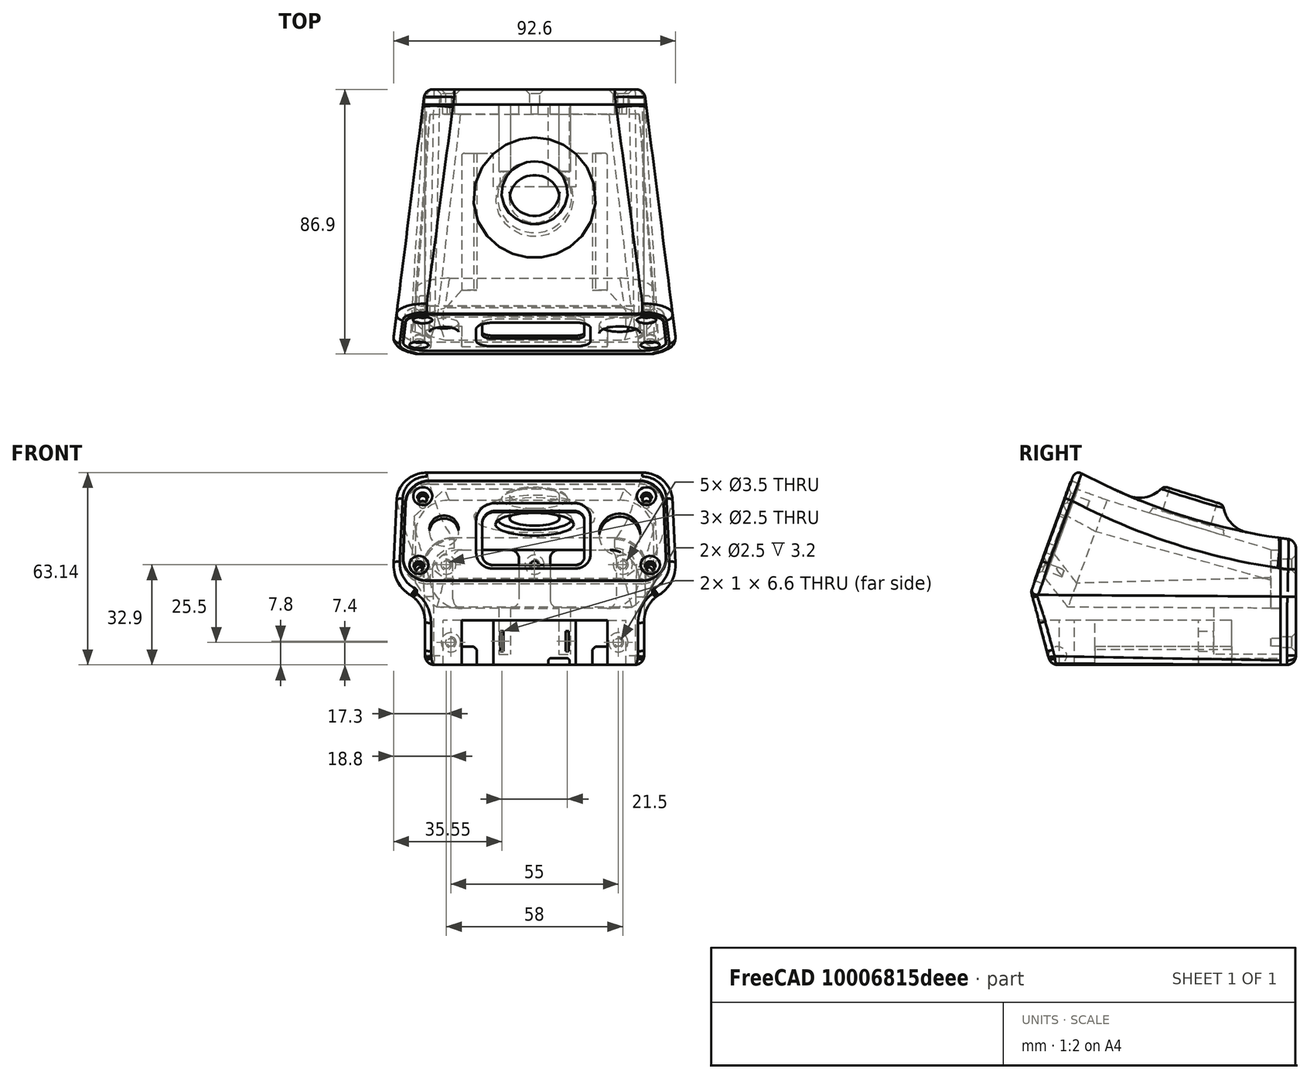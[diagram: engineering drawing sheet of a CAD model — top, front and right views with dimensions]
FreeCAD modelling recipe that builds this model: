
FCSTD DOCUMENT  (FreeCAD 2021.412R24301 +3461 (Git))
Label: solder_station4
License: All rights reserved
LicenseURL: http://en.wikipedia.org/wiki/All_rights_reserved
objects: Sketcher::SketchObject×18, PartDesign::Pocket×8, PartDesign::Fillet×6, Part::FeaturePython×3, App::DocumentObjectGroup×3, PartDesign::Chamfer×3, PartDesign::Body×3, PartDesign::FeatureBase×2, PartDesign::Pad×2, Mesh::Feature×2, Spreadsheet::Sheet×1, Part::Plane×1, Part::Loft×1, Part::Extrusion×1, Part::MultiCommon×1, PartDesign::SubtractiveLoft×1, PartDesign::Revolution×1, PartDesign::Groove×1, App::Part×1
note: 98 computed .brp shape members not serialized (recipe doc carries the construction recipe); baked Part::Feature solids carry a one-line shape summary decoded from their .brp

FEATURE [Sketcher::SketchObject] Sketch  label="RearSupport"
  AttachmentOffset = pos=(0,0,-37.8) rot=(0,0,1;0rad)
  FullyConstrained = true
  MapMode = 5
  Placement = pos=(0,37.8,8.4e-15) rot=(1,0,0;1.5708rad)
  Support = -> [XZ_Plane005]
  expr: .AttachmentOffset.Base.z = -<<param>>.mid_depth / 2 + <<param>>.wall
  expr: .Constraints[24] = 3
  expr: .Constraints[37] = <<param>>.bottom_height
  expr: .Constraints[38] = <<param>>.floor
  expr: .Constraints[39] = <<param>>.rear_height - <<param>>.wall
  expr: .Constraints[47] = <<param>>.reart_screw_width2
  expr: .Constraints[48] = <<param>>.rear_screw_width1
  expr: .Constraints[49] = <<param>>.screw_hole
  expr: .Constraints[50] = <<param>>.rear_screw_height
  expr: .Constraints[51] = <<param>>.rear_screw_height
  expr: .Constraints[52] = <<param>>.rear_screw_offset
  sketch-geometry (22):
    g0: LineSegment StartX=-23.8 StartY=13.8 StartZ=0 EndX=-8.1 EndY=13.8 EndZ=0
    g1: LineSegment StartX=26.8 StartY=10.8 StartZ=0 EndX=26.8 EndY=-2.4 EndZ=0
    g2: LineSegment StartX=23.8 StartY=-5.4 StartZ=0 EndX=8.1 EndY=-5.4 EndZ=0
    g3: LineSegment StartX=-26.8 StartY=-2.4 StartZ=0 EndX=-26.8 EndY=10.8 EndZ=0
    g4: LineSegment StartX=-5.1 StartY=10.8 StartZ=0 EndX=-5.1 EndY=-2.4 EndZ=0
    g5: LineSegment StartX=5.1 StartY=10.8 StartZ=0 EndX=5.1 EndY=-2.4 EndZ=0
    g6: LineSegment StartX=8.1 StartY=13.8 StartZ=0 EndX=23.8 EndY=13.8 EndZ=0
    g7: LineSegment StartX=-8.1 StartY=-5.4 StartZ=0 EndX=-23.8 EndY=-5.4 EndZ=0
    g8: ArcOfCircle CenterX=-8.1 CenterY=10.8 CenterZ=0 NormalX=0 NormalY=0 NormalZ=1 AngleXU=0 Radius=3 StartAngle=0 EndAngle=1.5708
    g9: ArcOfCircle CenterX=8.1 CenterY=10.8 CenterZ=0 NormalX=0 NormalY=0 NormalZ=1 AngleXU=0 Radius=3 StartAngle=1.5708 EndAngle=3.14159
    g10: ArcOfCircle CenterX=-8.1 CenterY=-2.4 CenterZ=0 NormalX=0 NormalY=0 NormalZ=1 AngleXU=0 Radius=3 StartAngle=4.71239 EndAngle=6.28319
    g11: ArcOfCircle CenterX=8.1 CenterY=-2.4 CenterZ=0 NormalX=0 NormalY=0 NormalZ=1 AngleXU=0 Radius=3 StartAngle=3.14159 EndAngle=4.71239
    g12: ArcOfCircle CenterX=-23.8 CenterY=10.8 CenterZ=0 NormalX=0 NormalY=0 NormalZ=1 AngleXU=0 Radius=3 StartAngle=1.5708 EndAngle=3.14159
    g13: ArcOfCircle CenterX=-23.8 CenterY=-2.4 CenterZ=0 NormalX=0 NormalY=0 NormalZ=1 AngleXU=0 Radius=3 StartAngle=3.14159 EndAngle=4.71239
    g14: ArcOfCircle CenterX=23.8 CenterY=10.8 CenterZ=0 NormalX=0 NormalY=0 NormalZ=1 AngleXU=0 Radius=3 StartAngle=0 EndAngle=1.5708
    g15: ArcOfCircle CenterX=23.8 CenterY=-2.4 CenterZ=0 NormalX=0 NormalY=0 NormalZ=1 AngleXU=0 Radius=3 StartAngle=4.71239 EndAngle=6.28319
    g16: Circle [constr] CenterX=0 CenterY=-24 CenterZ=0 NormalX=0 NormalY=0 NormalZ=1 AngleXU=0 Radius=3
    g17: Circle CenterX=0 CenterY=8.9 CenterZ=0 NormalX=0 NormalY=0 NormalZ=1 AngleXU=0 Radius=1.25
    g18: Circle CenterX=-29 CenterY=8.9 CenterZ=0 NormalX=0 NormalY=0 NormalZ=1 AngleXU=0 Radius=1.25
    g19: Circle CenterX=-27.5 CenterY=-16.6 CenterZ=0 NormalX=0 NormalY=0 NormalZ=1 AngleXU=0 Radius=1.25
    g20: Circle CenterX=27.5 CenterY=-16.6 CenterZ=0 NormalX=0 NormalY=0 NormalZ=1 AngleXU=0 Radius=1.25
    g21: Circle CenterX=29 CenterY=8.9 CenterZ=0 NormalX=0 NormalY=0 NormalZ=1 AngleXU=0 Radius=1.25
  constraints (53):
    c: Horizontal(g0)
    c: Horizontal(g2)
    c: Vertical(g1)
    c: Vertical(g3)
    c: Vertical(g4)
    c: Vertical(g5)
    c: Tangent(g0,g6)
    c: Tangent(g2,g7)
    c: Tangent(g0,g8) = 1.5708
    c: Tangent(g4,g8) = 1.5708
    c: Tangent(g5,g9) = -1.5708
    c: Tangent(g6,g9) = 1.5708
    c: Tangent(g7,g10) = 1.5708
    c: Tangent(g4,g10) = 1.5708
    c: Tangent(g5,g11) = -1.5708
    c: Tangent(g2,g11) = 1.5708
    c: Tangent(g0,g12) = 1.5708
    c: Tangent(g3,g12) = 1.5708
    c: Tangent(g3,g13) = 1.5708
    c: Tangent(g7,g13) = 1.5708
    c: Tangent(g6,g14) = 1.5708
    c: Tangent(g1,g14) = 1.5708
    c: Tangent(g1,g15) = 1.5708
    c: Tangent(g2,g15) = 1.5708
    c: Radius(g9) = 3
    c: Equal(g12,g13)
    c: Equal(g13,g10)
    c: Equal(g10,g8)
    c: Equal(g11,g15)
    c: Equal(g15,g14)
    c: Equal(g14,g9)
    c: DistanceX(g4,g-1) = 5.1
    c: DistanceX(g5,g1) = 21.7
    c: Symmetric(g4,g5,g-2)
    c: Equal(g7,g2)
    c: PointOnObject(g16,g-2)
    c: Radius(g16) = 3
    c: DistanceY(g16,g-1) = 24
    c: DistanceY(g16,g2) = 18.6
    c: DistanceY(g16,g6) = 37.8
    c: PointOnObject(g17,g-2)
    c: Equal(g21,g18)
    c: Equal(g18,g19)
    c: Equal(g19,g20)
    c: Equal(g18,g17)
    c: Symmetric(g20,g19,g-2)
    c: Symmetric(g18,g21,g-2)
    c: DistanceX(g19,g20) = 55
    c: DistanceX(g18,g21) = 58
    c: Diameter(g19) = 2.5
    c: DistanceY(g20,g21) = 25.5
    c: DistanceY(g20,g17) = 25.5
    c: DistanceY(g16,g19) = 7.4
FEATURE [Spreadsheet::Sheet] Spreadsheet  label="param"
  PythonMode = false
  cells = A1=Body; B2=top_depth; C2(top_depth)=70; B3=mid_depth; C3(mid_depth)=82; D3=half is rear reference; B4=bottom_depth; C4(bottom_depth)=75; B6=bottom_width; C6(bottom_width)=72; B7=bottom_height; C7(bottom_height)=24; B8=bottom_angle; C8(bottom_angle)=15; B10=rear_width; C10(rear_width)=72; B11=rear_height; C11(rear_height)=41; B13=mid_width; C13(mid_width)=80; B14=mid_height; C14(mid_height)=50; B16=front_width1; C16(front_width1)=91; D16=@top; E16=upper; B17=front_width2; C17(front_width2)=94; D17=@mid; E17=lower; B18=front_height; C18(front_height)=64; B19=front_angle; C19(front_angle)=20; B21=wall; C21(wall)=3.2; B22=radius_big; C22(radius_big)=10; B23=radius_small; C23(radius_small)=3; B24=arch; C24(arch)=200; A26=Button; B27=button_offset; C27(button_offset)=10; B28=button_inside_dia; C28(button_inside_dia)=20; B29=button_outside_dia; C29(button_outside_dia)=22; B30=button_height; C30(button_height)=24; B31=button_extension; C31(button_extension)=8; B32=button_fillet; C32(button_fillet)=12; B33=button_angle; C33(button_angle)=-17; B34=button_hole; C34(button_hole)=16.4; B35=button_hole_center; C35(button_hole_center)=-0.5; A37=Battery Cuts; B38=batt_carveout; C38(batt_carveout)=14.6; B39=batt_rail; C39(batt_rail)=6; B40=batt_rail_length; C40(batt_rail_length)=45; A42=Terminals; B43=terminal_height; C43(terminal_height)=6.6; B44=terminal_thickness; C44(terminal_thickness)=1; B45=terminal_seperation; C45(terminal_seperation)=21.5; B46=terminal_offset; C46(terminal_offset)=4.5; B47=terminal_depth; C47(terminal_depth)=22; A49=Box Interior; B50=floor; C50(floor)=18.6; B51=rear_inside_width; C51(rear_inside_width)==C10 - C21; D51=calc; B52=rear_inside_height; C52(rear_inside_height)==C11 - C21; D52=calc; B53=mid_inside_width; C53(mid_inside_width)==C13; D53=calc; B54=mid_inside_height; C54(mid_inside_height)==C14 + 6; D54=calc; B55=front_inside_width1; C55(front_inside_width1)==C62 - C58 * 2; D55=calc; E55=upper; B56=front_inside_width2; C56(front_inside_width2)==C63 - C58 * 2; D56=calc; E56=lower; B57=front_inside_height; C57(front_inside_height)==C64 - C59 * 2; D57=calc; B58=front_width_lip_width; C58(front_width_lip_width)=3; B59=front_inside_lip_height; C59(front_inside_lip_height)=2; A61=Face; B62=face_width1; C62(face_width1)==84 + 1; B63=face_width2; C63(face_width2)==85.5 + 1; B64=face_height; C64(face_height)==34 + 1; B65=face_thickness; C65(face_thickness)=3; B66=face_radius; C66(face_radius)=8; B67=face_offset; C67(face_offset)=2.8; D67=2.8; A69=Screws; B70=screw_hole; C70(screw_hole)=2.5; B72=front_screw_width1; C72(front_screw_width1)=73.5; D72=upper; B73=front_screw_width2; C73(front_screw_width2)=76; D73=lower; B74=front_screw_height; C74(front_screw_height)=24; B75=front_screw_offset; C75(front_screw_offset)=5.5; B77=rear_screw_width1; C77(rear_screw_width1)=58; B78=reart_screw_width2; C78(reart_screw_width2)=55; B79=rear_screw_height; C79(rear_screw_height)=25.5; B80=rear_screw_offset; C80(rear_screw_offset)=7.4; A82=Back; B83=back_thickness; C83(back_thickness)=5
FEATURE [Sketcher::SketchObject] Sketch008  label="SketchButtonHole"
  AttachmentOffset = pos=(0,-0.5,24) rot=(1,0,0;-0.296706rad)
  FullyConstrained = true
  MapMode = 5
  Placement = pos=(0,-0.5,24) rot=(1,0,0;5.98648rad)
  Support = -> [XY_Plane005]
  expr: .AttachmentOffset.Base.y = <<param>>.button_hole_center
  expr: .AttachmentOffset.Base.z = <<param>>.button_height
  expr: .AttachmentOffset.Rotation.Angle = <<param>>.button_angle
  expr: .Constraints[0] = <<param>>.button_hole
  expr: .Constraints[2] = <<param>>.button_offset
  sketch-geometry (1):
    g0: Circle CenterX=0 CenterY=10 CenterZ=0 NormalX=0 NormalY=0 NormalZ=1 AngleXU=0 Radius=8.2
  constraints (3):
    c: Diameter(g0) = 16.4
    c: PointOnObject(g0,g-2)
    c: DistanceY(g-1,g0) = 10
FEATURE [Sketcher::SketchObject] Sketch012  label="SketchSide"
  AttachmentOffset = pos=(2.5,0,0) rot=(0,0,1;0rad)
  FullyConstrained = true
  MapMode = 5
  Placement = pos=(6e-16,2.5,-6e-16) rot=(0.57735,0.57735,0.57735;2.0944rad)
  Support = -> [YZ_Plane006]
  expr: .AttachmentOffset.Base.x = <<param>>.back_thickness / 2
  expr: .Constraints[14] = <<param>>.bottom_height
  expr: .Constraints[15] = <<param>>.radius_small
  expr: .Constraints[16] = 90 - <<param>>.bottom_angle
  expr: .Constraints[17] = 90 - <<param>>.front_angle
  expr: .Constraints[21] = <<param>>.front_height
  expr: .Constraints[4] = <<param>>.rear_height - <<param>>.bottom_height
  expr: .Constraints[5] = <<param>>.arch
  expr: .Constraints[6] = <<param>>.mid_depth + <<param>>.back_thickness
  sketch-geometry (7):
    g0: LineSegment StartX=43.5 StartY=0 StartZ=0 EndX=43.5 EndY=17 EndZ=0
    g1: LineSegment StartX=-43.5 StartY=0 StartZ=0 EndX=-28.9412 EndY=40 EndZ=0
    g2: ArcOfCircle CenterX=66.6993 CenterY=215.65 CenterZ=0 NormalX=0 NormalY=0 NormalZ=1 AngleXU=0 Radius=200 StartAngle=4.21378 EndAngle=4.59613
    g3: LineSegment StartX=-43.5 StartY=0 StartZ=0 EndX=-37.665 EndY=-21.7765 EndZ=0
    g4: LineSegment StartX=-34.7673 StartY=-24 StartZ=0 EndX=43.5 EndY=-24 EndZ=0
    g5: LineSegment StartX=43.5 StartY=-24 StartZ=0 EndX=43.5 EndY=0 EndZ=0
    g6: ArcOfCircle CenterX=-34.7672 CenterY=-21 CenterZ=0 NormalX=0 NormalY=0 NormalZ=1 AngleXU=0 Radius=3 StartAngle=3.4034 EndAngle=4.71238
  constraints (22):
    c: PointOnObject(g1,g-1)
    c: Vertical(g0)
    c: Coincident(g2,g0)
    c: Symmetric(g1,g0,g-2)
    c: DistanceY(g0,g0) = 17
    c: Radius(g2) = 200
    c: DistanceX(g1,g0) = 87
    c: Horizontal(g4)
    c: Coincident(g5,g4)
    c: Vertical(g5)
    c: Coincident(g6,g3)
    c: Coincident(g6,g4)
    c: Tangent(g6,g4)
    c: Tangent(g6,g3)
    c: DistanceY(g4,g-1) = 24
    c: Radius(g6) = 3
    c: Angle(g3,g-1) = 1.309
    c: Angle(g-1,g1) = 1.22173
    c: Coincident(g3,g1)
    c: Coincident(g5,g0)
    c: Coincident(g2,g1)
    c: DistanceY(g4,g1) = 64
FEATURE [Sketcher::SketchObject] Sketch018  label="SketchBat1"
  AttachmentOffset = pos=(0,0,-24) rot=(0,0,1;0rad)
  FullyConstrained = true
  MapMode = 5
  Placement = pos=(0,0,-24) rot=(0,0,1;0rad)
  Support = -> [XY_Plane005]
  expr: .AttachmentOffset.Base.z = -<<param>>.bottom_height
  expr: .Constraints[63] = <<param>>.batt_rail_length
  expr: .Constraints[64] = <<param>>.mid_depth / 2
  sketch-geometry (21):
    g0: LineSegment StartX=-24 StartY=-41.7082 StartZ=0 EndX=24 EndY=-41.7082 EndZ=0
    g1: LineSegment StartX=24 StartY=-41.7082 StartZ=0 EndX=24 EndY=-31.7082 EndZ=0
    g2: LineSegment StartX=24 StartY=-31.7082 StartZ=0 EndX=30 EndY=-31.7082 EndZ=0
    g3: LineSegment StartX=30 StartY=-31.7082 StartZ=0 EndX=30 EndY=-26.7082 EndZ=0
    g4: LineSegment StartX=30 StartY=-26.7082 StartZ=0 EndX=24 EndY=-20 EndZ=0
    g5: LineSegment StartX=24 StartY=-20 StartZ=0 EndX=24 EndY=24 EndZ=0
    g6: LineSegment StartX=13.5 StartY=24 StartZ=0 EndX=13.5 EndY=14 EndZ=0
    g7: LineSegment StartX=13.5 StartY=14 StartZ=0 EndX=-13.5 EndY=14 EndZ=0
    g8: LineSegment StartX=-13.5 StartY=14 StartZ=0 EndX=-13.5 EndY=24 EndZ=0
    g9: LineSegment StartX=-24 StartY=24 StartZ=0 EndX=-24 EndY=-20 EndZ=0
    g10: LineSegment StartX=-24 StartY=-20 StartZ=0 EndX=-30 EndY=-26.7082 EndZ=0
    g11: LineSegment StartX=-30 StartY=-26.7082 StartZ=0 EndX=-30 EndY=-31.7082 EndZ=0
    g12: LineSegment StartX=-30 StartY=-31.7082 StartZ=0 EndX=-24 EndY=-31.7082 EndZ=0
    g13: LineSegment StartX=-24 StartY=-31.7082 StartZ=0 EndX=-24 EndY=-41.7082 EndZ=0
    g14: Circle [constr] CenterX=0 CenterY=41 CenterZ=0 NormalX=0 NormalY=0 NormalZ=1 AngleXU=0 Radius=4
    g15: ArcOfCircle CenterX=-14.5 CenterY=24 CenterZ=0 NormalX=0 NormalY=0 NormalZ=1 AngleXU=0 Radius=1 StartAngle=6.28318 EndAngle=7.85399
    g16: LineSegment StartX=-23 StartY=25 StartZ=0 EndX=-14.5 EndY=25 EndZ=0
    g17: LineSegment StartX=14.5 StartY=25 StartZ=0 EndX=23 EndY=25 EndZ=0
    g18: ArcOfCircle CenterX=-23 CenterY=24 CenterZ=0 NormalX=0 NormalY=0 NormalZ=1 AngleXU=0 Radius=1 StartAngle=1.57079 EndAngle=3.1416
    g19: ArcOfCircle CenterX=14.5 CenterY=24 CenterZ=0 NormalX=0 NormalY=0 NormalZ=1 AngleXU=0 Radius=1 StartAngle=1.5708 EndAngle=3.14159
    g20: ArcOfCircle CenterX=23 CenterY=24 CenterZ=0 NormalX=0 NormalY=0 NormalZ=1 AngleXU=0 Radius=1.00001 StartAngle=2.75124e-06 EndAngle=1.5708
  constraints (65):
    c: Horizontal(g0)
    c: Coincident(g1,g0)
    c: Vertical(g1)
    c: Coincident(g2,g1)
    c: Horizontal(g2)
    c: Coincident(g3,g2)
    c: Coincident(g3,g4)
    c: Vertical(g5)
    c: Coincident(g6,g7)
    c: Coincident(g7,g8)
    c: Vertical(g8)
    c: Vertical(g9)
    c: Coincident(g10,g11)
    c: Vertical(g11)
    c: Coincident(g11,g12)
    c: Horizontal(g12)
    c: Coincident(g12,g13)
    c: Equal(g6,g8)
    c: Equal(g5,g9)
    c: Equal(g4,g10)
    c: Equal(g3,g11)
    c: Equal(g12,g2)
    c: Equal(g1,g13)
    c: Coincident(g13,g0)
    c: Vertical(g13)
    c: DistanceX(g7,g7) = 27
    c: Symmetric(g7,g6,g-2)
    c: Distance(g4) = 9
    c: Vertical(g3)
    c: DistanceY(g3,g3) = 5
    c: DistanceX(g2,g2) = 6
    c: DistanceY(g1,g1) = 10
    c: DistanceX(g0,g0) = 48
    c: PointOnObject(g14,g-2)
    c: Coincident(g9,g10)
    c: Coincident(g5,g4)
    c: Coincident(g15,g8)
    c: Coincident(g16,g15)
    c: Tangent(g15,g8)
    c: Horizontal(g16)
    c: Horizontal(g17)
    c: DistanceX(g9,g5) = 48
    c: Symmetric(g4,g9,g-2)
    c: Equal(g16,g17)
    c: Coincident(g18,g9)
    c: Coincident(g18,g16)
    c: Equal(g18,g15)
    c: Tangent(g18,g16)
    c: Tangent(g18,g9)
    c: DistanceY(g6,g17) = 11
    c: Vertical(g6)
    c: Coincident(g19,g6)
    c: Coincident(g19,g17)
    c: Coincident(g20,g17)
    c: Coincident(g20,g5)
    c: Tangent(g20,g17)
    c: Tangent(g20,g5)
    c: Tangent(g19,g6)
    c: Tangent(g19,g17)
    c: Equal(g15,g19)
    c: Radius(g19) = 1
    c: Radius(g14) = 4
    c: DistanceY(g15,g14) = 16
    c: DistanceY(g9,g16) = 45
    c: DistanceY(g-1,g14) = 41
FEATURE [Sketcher::SketchObject] Sketch019  label="SketchBat2"
  AttachmentOffset = pos=(0,0,-25) rot=(0,0,1;0rad)
  FullyConstrained = true
  MapMode = 5
  Placement = pos=(0,25,5.6e-15) rot=(1,0,0;1.5708rad)
  Support = -> [XZ_Plane005]
  expr: .AttachmentOffset.Base.z = -<<param>>.mid_depth / 2 + 16
  expr: .Constraints[17] = <<param>>.bottom_height
  expr: .Constraints[18] = <<param>>.batt_rail
  expr: .Constraints[19] = 48.01mm
  sketch-geometry (10):
    g0: LineSegment StartX=-24.005 StartY=-18 StartZ=0 EndX=-20.005 EndY=-18 EndZ=0
    g1: LineSegment StartX=-19.005 StartY=-24 StartZ=0 EndX=-24.005 EndY=-24 EndZ=0
    g2: LineSegment StartX=-24.005 StartY=-24 StartZ=0 EndX=-24.005 EndY=-18 EndZ=0
    g3: LineSegment StartX=24.005 StartY=-18 StartZ=0 EndX=20.005 EndY=-18 EndZ=0
    g4: LineSegment StartX=19.005 StartY=-24 StartZ=0 EndX=24.005 EndY=-24 EndZ=0
    g5: LineSegment StartX=24.005 StartY=-24 StartZ=0 EndX=24.005 EndY=-18 EndZ=0
    g6: LineSegment StartX=-19.005 StartY=-19 StartZ=0 EndX=-19.005 EndY=-24 EndZ=0
    g7: LineSegment StartX=19.005 StartY=-24 StartZ=0 EndX=19.005 EndY=-19 EndZ=0
    g8: LineSegment StartX=-20.005 StartY=-18 StartZ=0 EndX=-19.005 EndY=-19 EndZ=0
    g9: LineSegment StartX=19.005 StartY=-19 StartZ=0 EndX=20.005 EndY=-18 EndZ=0
  constraints (29):
    c: Coincident(g1,g2)
    c: Coincident(g2,g0)
    c: Horizontal(g0)
    c: Horizontal(g1)
    c: Vertical(g2)
    c: Coincident(g4,g5)
    c: Coincident(g5,g3)
    c: Horizontal(g3)
    c: Horizontal(g4)
    c: Vertical(g5)
    c: Coincident(g6,g1)
    c: Vertical(g6)
    c: Equal(g1,g4)
    c: Coincident(g7,g4)
    c: Vertical(g7)
    c: Equal(g6,g7)
    c: Symmetric(g1,g4,g-2)
    c: DistanceY(g1,g-1) = 24
    c: DistanceY(g4,g3) = 6
    c: DistanceX(g1,g4) = 48.01
    c: DistanceX(g4,g4) = 5
    c: Coincident(g8,g0)
    c: Coincident(g8,g6)
    c: Coincident(g9,g7)
    c: Coincident(g9,g3)
    c: Equal(g0,g3)
    c: Equal(g2,g5)
    c: DistanceX(g0,g0) = 4
    c: DistanceY(g1,g6) = 5
FEATURE [Sketcher::SketchObject] Sketch021  label="SketchButton"
  AttachmentOffset = pos=(10,24,0) rot=(0,0,1;-0.296706rad)
  FullyConstrained = true
  MapMode = 5
  Placement = pos=(-3.1e-15,10,24) rot=(-0.51122,-0.690875,-0.51122;4.35074rad)
  Support = -> [YZ_Plane005]
  expr: .AttachmentOffset.Base.x = <<param>>.button_offset
  expr: .AttachmentOffset.Base.y = <<param>>.button_height
  expr: .AttachmentOffset.Rotation.Angle = <<param>>.button_angle
  expr: .Constraints[6] = <<param>>.button_extension
  expr: .Constraints[7] = <<param>>.button_outside_dia / 2
  sketch-geometry (5):
    g0: LineSegment StartX=0 StartY=0 StartZ=0 EndX=0 EndY=8 EndZ=0
    g1: LineSegment StartX=0 StartY=8 StartZ=0 EndX=9 EndY=8 EndZ=0
    g2: LineSegment StartX=0 StartY=0 StartZ=0 EndX=11 EndY=0 EndZ=0
    g3: LineSegment StartX=11 StartY=0 StartZ=0 EndX=11 EndY=6 EndZ=0
    g4: ArcOfCircle CenterX=9 CenterY=6 CenterZ=0 NormalX=0 NormalY=0 NormalZ=1 AngleXU=0 Radius=2 StartAngle=1.123e-13 EndAngle=1.5708
  constraints (13):
    c: Coincident(g0,g-1)
    c: PointOnObject(g0,g-2)
    c: Coincident(g1,g0)
    c: Horizontal(g1)
    c: Coincident(g2,g0)
    c: Horizontal(g2)
    c: DistanceY(g0,g0) = 8
    c: DistanceX(g2,g2) = 11
    c: Coincident(g3,g2)
    c: Vertical(g3)
    c: Radius(g4) = 2
    c: Tangent(g4,g3) = -1.5708
    c: Tangent(g4,g1) = 1.5708
FEATURE [Sketcher::SketchObject] Sketch022  label="SketchRearInside"
  AttachmentOffset = pos=(0,0,-37.8) rot=(0,0,1;0rad)
  FullyConstrained = true
  MapMode = 5
  Placement = pos=(0,37.8,8.4e-15) rot=(1,0,0;1.5708rad)
  Support = -> [XZ_Plane005]
  expr: .AttachmentOffset.Base.z = -<<param>>.mid_depth / 2 + <<param>>.wall
  expr: .Constraints[12] = <<param>>.radius_big
  expr: .Constraints[18] = <<param>>.rear_inside_width
  expr: .Constraints[26] = <<param>>.bottom_height
  expr: .Constraints[27] = <<param>>.rear_inside_height
  expr: .Constraints[29] = <<param>>.floor
  sketch-geometry (9):
    g0: LineSegment StartX=-34.4 StartY=3.80003 StartZ=0 EndX=-34.4 EndY=4.59997 EndZ=0
    g1: LineSegment StartX=-24.4 StartY=-5.4 StartZ=0 EndX=24.4 EndY=-5.4 EndZ=0
    g2: LineSegment StartX=34.4 StartY=4.59997 StartZ=0 EndX=34.4 EndY=3.80003 EndZ=0
    g3: LineSegment StartX=-24.4 StartY=13.8 StartZ=0 EndX=24.4 EndY=13.8 EndZ=0
    g4: ArcOfCircle CenterX=24.4 CenterY=3.8 CenterZ=0 NormalX=0 NormalY=0 NormalZ=1 AngleXU=0 Radius=10 StartAngle=3.49138e-06 EndAngle=1.57079
    g5: ArcOfCircle CenterX=24.4 CenterY=4.6 CenterZ=0 NormalX=0 NormalY=0 NormalZ=1 AngleXU=0 Radius=10 StartAngle=4.71239 EndAngle=6.28318
    g6: ArcOfCircle CenterX=-24.4 CenterY=3.8 CenterZ=0 NormalX=0 NormalY=0 NormalZ=1 AngleXU=0 Radius=10 StartAngle=1.5708 EndAngle=3.14159
    g7: ArcOfCircle CenterX=-24.4 CenterY=4.6 CenterZ=0 NormalX=0 NormalY=0 NormalZ=1 AngleXU=0 Radius=10 StartAngle=3.1416 EndAngle=4.71239
    g8: Circle [constr] CenterX=0 CenterY=-24 CenterZ=0 NormalX=0 NormalY=0 NormalZ=1 AngleXU=0 Radius=3
  constraints (30):
    c: Vertical(g0)
    c: Horizontal(g1)
    c: Vertical(g2)
    c: Horizontal(g3)
    c: Equal(g3,g1)
    c: Equal(g0,g2)
    c: Coincident(g4,g3)
    c: Coincident(g4,g2)
    c: Coincident(g5,g2)
    c: Coincident(g5,g1)
    c: Coincident(g6,g0)
    c: Coincident(g6,g3)
    c: Radius(g6) = 10
    c: Equal(g6,g4)
    c: Equal(g4,g5)
    c: Coincident(g7,g1)
    c: Coincident(g7,g0)
    c: Equal(g5,g7)
    c: DistanceX(g0,g2) = 68.8
    c: Symmetric(g0,g2,g-2)
    c: Tangent(g4,g2)
    c: Tangent(g4,g3)
    c: Tangent(g5,g2)
    c: Tangent(g5,g1)
    c: Tangent(g6,g3)
    c: PointOnObject(g8,g-2)
    c: DistanceY(g8,g-1) = 24
    c: DistanceY(g8,g3) = 37.8
    c: Radius(g8) = 3
    c: DistanceY(g8,g1) = 18.6
FEATURE [Sketcher::SketchObject] Sketch023  label="SketchFrontInside"
  AttachmentOffset = pos=(0,0,38) rot=(1,0,0;-0.349066rad)
  FullyConstrained = true
  MapMode = 5
  Placement = pos=(0,-38,-8.4e-15) rot=(-1,0,0;5.06145rad)
  Support = -> [XZ_Plane005]
  expr: .AttachmentOffset.Base.z = <<param>>.mid_depth / 2 - <<param>>.face_thickness
  expr: .AttachmentOffset.Rotation.Angle = -<<param>>.front_angle
  expr: .Constraints[19] = <<param>>.front_inside_width2
  expr: .Constraints[1] = <<param>>.front_inside_width1
  expr: .Constraints[20] = <<param>>.front_inside_width2 / 2
  expr: .Constraints[21] = <<param>>.face_offset + <<param>>.front_inside_lip_height
  expr: .Constraints[2] = <<param>>.front_inside_height
  sketch-geometry (8):
    g0: LineSegment StartX=-29.5 StartY=4.8 StartZ=0 EndX=29.5 EndY=4.8 EndZ=0
    g1: LineSegment StartX=29.5 StartY=35.8 StartZ=0 EndX=-29.5 EndY=35.8 EndZ=0
    g2: LineSegment StartX=-39.5 StartY=26.3677 StartZ=0 EndX=-40.25 EndY=13.3677 EndZ=0
    g3: LineSegment StartX=-39.5 StartY=26.3677 StartZ=0 EndX=-29.5 EndY=35.8 EndZ=0
    g4: LineSegment StartX=29.5 StartY=35.8 StartZ=0 EndX=39.5 EndY=26.3677 EndZ=0
    g5: LineSegment StartX=40.25 StartY=13.3677 StartZ=0 EndX=29.5 EndY=4.8 EndZ=0
    g6: LineSegment StartX=-40.25 StartY=13.3677 StartZ=0 EndX=-29.5 EndY=4.8 EndZ=0
    g7: LineSegment StartX=39.5 StartY=26.3677 StartZ=0 EndX=40.25 EndY=13.3677 EndZ=0
  constraints (22):
    c: Symmetric(g0,g0,g-2)
    c: DistanceX(g2,g4) = 79
    c: DistanceY(g0,g1) = 31
    c: Symmetric(g1,g1,g-2)
    c: Coincident(g3,g2)
    c: Coincident(g3,g1)
    c: Coincident(g4,g1)
    c: Coincident(g5,g0)
    c: Coincident(g6,g2)
    c: Coincident(g6,g0)
    c: Equal(g3,g6)
    c: Equal(g6,g5)
    c: Equal(g5,g4)
    c: Coincident(g7,g4)
    c: Coincident(g7,g5)
    c: DistanceY(g7,g7) = 13
    c: Equal(g7,g2)
    c: Equal(g1,g0)
    c: DistanceX(g1,g1) = 59
    c: DistanceX(g2,g5) = 80.5
    c: DistanceX(g2,g-1) = 40.25
    c: DistanceY(g-1,g0) = 4.8
FEATURE [Sketcher::SketchObject] Sketch024  label="SketchFaceCut"
  AttachmentOffset = pos=(0,0,38) rot=(1,0,0;-0.349066rad)
  FullyConstrained = true
  MapMode = 5
  Placement = pos=(0,-38,-8.4e-15) rot=(-1,0,0;5.06145rad)
  Support = -> [XZ_Plane005]
  expr: .AttachmentOffset.Base.z = <<param>>.mid_depth / 2 - <<param>>.face_thickness
  expr: .AttachmentOffset.Rotation.Angle = -<<param>>.front_angle
  expr: .Constraints[13] = <<param>>.face_radius
  expr: .Constraints[22] = <<param>>.face_width1
  expr: .Constraints[23] = <<param>>.face_width2
  expr: .Constraints[24] = <<param>>.face_offset
  expr: .Constraints[25] = <<param>>.face_height
  sketch-geometry (8):
    g0: LineSegment StartX=-34.5062 StartY=37.8 StartZ=0 EndX=34.5063 EndY=37.8 EndZ=0
    g1: LineSegment StartX=42.5001 StartY=30.1155 StartZ=0 EndX=43.25 EndY=11.1155 EndZ=0
    g2: LineSegment StartX=35.2562 StartY=2.8 StartZ=0 EndX=-35.2562 EndY=2.8 EndZ=0
    g3: LineSegment StartX=-43.25 StartY=11.1156 StartZ=0 EndX=-42.4999 EndY=30.1156 EndZ=0
    g4: ArcOfCircle CenterX=34.5063 CenterY=29.8 CenterZ=0 NormalX=0 NormalY=0 NormalZ=1 AngleXU=0 Radius=8 StartAngle=0.0394514 EndAngle=1.5708
    g5: ArcOfCircle CenterX=35.2563 CenterY=10.8 CenterZ=0 NormalX=0 NormalY=0 NormalZ=1 AngleXU=0 Radius=8 StartAngle=4.71239 EndAngle=6.32264
    g6: ArcOfCircle CenterX=-34.5062 CenterY=29.8 CenterZ=0 NormalX=0 NormalY=0 NormalZ=1 AngleXU=0 Radius=8 StartAngle=1.5708 EndAngle=3.10214
    g7: ArcOfCircle CenterX=-35.2562 CenterY=10.8 CenterZ=0 NormalX=0 NormalY=0 NormalZ=1 AngleXU=0 Radius=8 StartAngle=3.10214 EndAngle=4.71239
  constraints (27):
    c: Horizontal(g0)
    c: Coincident(g4,g0)
    c: Coincident(g4,g1)
    c: Coincident(g5,g1)
    c: Coincident(g5,g2)
    c: Coincident(g6,g0)
    c: Coincident(g6,g3)
    c: Coincident(g7,g3)
    c: Coincident(g7,g2)
    c: Equal(g1,g3)
    c: Equal(g4,g6)
    c: Equal(g6,g7)
    c: Equal(g7,g5)
    c: Radius(g4) = 8
    c: Tangent(g6,g3)
    c: Tangent(g7,g3)
    c: Tangent(g7,g2)
    c: Tangent(g6,g0)
    c: Tangent(g4,g0)
    c: Tangent(g4,g1)
    c: Tangent(g5,g1)
    c: Tangent(g5,g2)
    c: DistanceX(g3,g1) = 85
    c: DistanceX(g3,g1) = 86.5
    c: DistanceY(g-1,g2) = 2.8
    c: DistanceY(g2,g0) = 35
    c: Symmetric(g2,g2,g-2)
FEATURE [Sketcher::SketchObject] Sketch025  label="SketchMidInside"
  AttachmentOffset = pos=(0,0,27) rot=(1,0,0;-0.349066rad)
  FullyConstrained = true
  MapMode = 5
  Placement = pos=(0,-27,-6e-15) rot=(-1,0,0;5.06145rad)
  Support = -> [XZ_Plane005]
  expr: .AttachmentOffset.Base.z = <<param>>.mid_depth / 2 - 14
  expr: .AttachmentOffset.Rotation.Angle = -<<param>>.front_angle
  expr: .Constraints[10] = <<param>>.radius_big + 1
  expr: .Constraints[11] = <<param>>.floor
  expr: .Constraints[12] = Spreadsheet.mid_inside_width - 2
  expr: .Constraints[14] = <<param>>.mid_inside_height
  expr: .Constraints[23] = <<param>>.mid_width - 16
  expr: .Constraints[4] = <<param>>.bottom_height
  sketch-geometry (9):
    g0: LineSegment StartX=-28 StartY=32 StartZ=0 EndX=28 EndY=32 EndZ=0
    g1: LineSegment StartX=39 StartY=21 StartZ=0 EndX=39 EndY=3 EndZ=0
    g2: LineSegment StartX=32 StartY=-5.4 StartZ=0 EndX=-32 EndY=-5.4 EndZ=0
    g3: LineSegment StartX=-39 StartY=3 StartZ=0 EndX=-39 EndY=21 EndZ=0
    g4: Circle [constr] CenterX=0 CenterY=-24 CenterZ=0 NormalX=0 NormalY=0 NormalZ=1 AngleXU=0 Radius=3
    g5: ArcOfCircle CenterX=-28 CenterY=21 CenterZ=0 NormalX=0 NormalY=0 NormalZ=1 AngleXU=0 Radius=11 StartAngle=1.5708 EndAngle=3.14159
    g6: ArcOfCircle CenterX=28 CenterY=21 CenterZ=0 NormalX=0 NormalY=0 NormalZ=1 AngleXU=0 Radius=11 StartAngle=0 EndAngle=1.5708
    g7: ArcOfCircle CenterX=-17.5474 CenterY=13.7605 CenterZ=0 NormalX=0 NormalY=0 NormalZ=1 AngleXU=0 Radius=24 StartAngle=3.60651 EndAngle=4.06615
    g8: ArcOfCircle CenterX=17.5474 CenterY=13.7605 CenterZ=0 NormalX=0 NormalY=0 NormalZ=1 AngleXU=0 Radius=24 StartAngle=5.35863 EndAngle=5.81826
  constraints (25):
    c: Vertical(g1)
    c: Vertical(g3)
    c: PointOnObject(g4,g-2)
    c: Radius(g4) = 3
    c: DistanceY(g4,g-1) = 24
    c: Tangent(g3,g5) = 1.5708
    c: Tangent(g0,g5) = 1.5708
    c: Tangent(g0,g6) = 1.5708
    c: Tangent(g1,g6) = 1.5708
    c: Equal(g6,g5)
    c: Radius(g6) = 11
    c: DistanceY(g4,g2) = 18.6
    c: DistanceX(g3,g1) = 78
    c: Symmetric(g2,g2,g-2)
    c: DistanceY(g4,g0) = 56
    c: Symmetric(g0,g0,g-2)
    c: Equal(g3,g1)
    c: Coincident(g7,g2)
    c: Coincident(g8,g1)
    c: Coincident(g8,g2)
    c: Coincident(g7,g3)
    c: Equal(g8,g7)
    c: Radius(g8) = 24
    c: DistanceX(g2,g2) = 64
    c: DistanceY(g1,g1) = 18
FEATURE [Sketcher::SketchObject] Sketch026  label="SketchFrontScrews"
  AttachmentOffset = pos=(0,0,38) rot=(1,0,0;-0.349066rad)
  FullyConstrained = true
  MapMode = 5
  Placement = pos=(0,-38,-8.4e-15) rot=(-1,0,0;5.06145rad)
  Support = -> [XZ_Plane005]
  expr: .AttachmentOffset.Base.z = <<param>>.mid_depth / 2 - <<param>>.face_thickness
  expr: .AttachmentOffset.Rotation.Angle = -<<param>>.front_angle
  expr: .Constraints[0] = <<param>>.front_screw_width1
  expr: .Constraints[13] = <<param>>.screw_hole
  expr: .Constraints[1] = <<param>>.front_screw_width2
  expr: .Constraints[2] = <<param>>.front_screw_height
  expr: .Constraints[9] = <<param>>.face_offset + <<param>>.front_screw_offset
  sketch-geometry (6):
    g0: Circle CenterX=-36.75 CenterY=32.3 CenterZ=0 NormalX=0 NormalY=0 NormalZ=1 AngleXU=0 Radius=1.25
    g1: Circle CenterX=36.75 CenterY=32.3 CenterZ=0 NormalX=0 NormalY=0 NormalZ=1 AngleXU=0 Radius=1.25
    g2: Circle CenterX=-38 CenterY=8.3 CenterZ=0 NormalX=0 NormalY=0 NormalZ=1 AngleXU=0 Radius=1.25
    g3: Circle CenterX=38 CenterY=8.3 CenterZ=0 NormalX=0 NormalY=0 NormalZ=1 AngleXU=0 Radius=1.25
    g4: LineSegment [constr] StartX=-36.75 StartY=32.3 StartZ=0 EndX=36.75 EndY=32.3 EndZ=0
    g5: LineSegment [constr] StartX=-38 StartY=8.3 StartZ=0 EndX=38 EndY=8.3 EndZ=0
  constraints (14):
    c: DistanceX(g0,g1) = 73.5
    c: DistanceX(g2,g3) = 76
    c: DistanceY(g3,g1) = 24
    c: Coincident(g4,g0)
    c: Coincident(g4,g1)
    c: Coincident(g5,g2)
    c: Coincident(g5,g3)
    c: Symmetric(g2,g3,g-2)
    c: Symmetric(g0,g1,g-2)
    c: DistanceY(g-1,g3) = 8.3
    c: Equal(g0,g2)
    c: Equal(g2,g3)
    c: Equal(g3,g1)
    c: Diameter(g0) = 2.5
FEATURE [Sketcher::SketchObject] Sketch027  label="SketchButtonCarve"
  AttachmentOffset = pos=(10,22,0) rot=(0,0,1;-0.296706rad)
  FullyConstrained = true
  MapMode = 5
  Placement = pos=(-2.7e-15,10,22) rot=(-0.51122,-0.690875,-0.51122;4.35074rad)
  Support = -> [YZ_Plane005]
  expr: .AttachmentOffset.Base.x = <<param>>.button_offset
  expr: .AttachmentOffset.Base.y = <<param>>.button_height - 2
  expr: .AttachmentOffset.Rotation.Angle = <<param>>.button_angle
  expr: .Constraints[12] = <<param>>.button_hole / 2 + 10
  expr: .Constraints[6] = <<param>>.button_hole / 2 + 4
  sketch-geometry (4):
    g0: LineSegment StartX=0 StartY=2 StartZ=0 EndX=12.2 EndY=2 EndZ=0
    g1: ArcOfCircle CenterX=18.2 CenterY=3.09999 CenterZ=0 NormalX=0 NormalY=0 NormalZ=1 AngleXU=0 Radius=6.09999 StartAngle=3.32291 EndAngle=4.71239
    g2: LineSegment StartX=0 StartY=2 StartZ=0 EndX=0 EndY=-3 EndZ=0
    g3: LineSegment StartX=18.2 StartY=-3 StartZ=0 EndX=0 EndY=-3 EndZ=0
  constraints (13):
    c: Horizontal(g0)
    c: Coincident(g1,g0)
    c: Coincident(g2,g0)
    c: Coincident(g3,g1)
    c: Horizontal(g3)
    c: Tangent(g3,g1)
    c: DistanceX(g0,g0) = 12.2
    c: DistanceY(g2,g2) = 5
    c: Coincident(g2,g3)
    c: Vertical(g2)
    c: PointOnObject(g-1,g2)
    c: DistanceY(g2,g-1) = 3
    c: DistanceX(g3,g3) = 18.2
FEATURE [Sketcher::SketchObject] Sketch028  label="SketchTerminals"
  FullyConstrained = true
  MapMode = 5
  Placement = pos=(0,0,0) rot=(1,0,0;1.5708rad)
  Support = -> [XZ_Plane005]
  expr: .Constraints[18] = <<param>>.terminal_thickness
  expr: .Constraints[19] = <<param>>.terminal_height
  expr: .Constraints[22] = <<param>>.bottom_height
  expr: .Constraints[23] = <<param>>.terminal_offset
  expr: .Constraints[24] = <<param>>.terminal_seperation
  sketch-geometry (15):
    g0: LineSegment StartX=10.25 StartY=-12.9 StartZ=0 EndX=11.25 EndY=-12.9 EndZ=0
    g1: LineSegment StartX=11.25 StartY=-12.9 StartZ=0 EndX=11.25 EndY=-19.5 EndZ=0
    g2: LineSegment StartX=11.25 StartY=-19.5 StartZ=0 EndX=10.25 EndY=-19.5 EndZ=0
    g3: LineSegment StartX=10.25 StartY=-19.5 StartZ=0 EndX=10.25 EndY=-12.9 EndZ=0
    g4: LineSegment StartX=-10.25 StartY=-12.9 StartZ=0 EndX=-11.25 EndY=-12.9 EndZ=0
    g5: LineSegment StartX=-11.25 StartY=-12.9 StartZ=0 EndX=-11.25 EndY=-19.5 EndZ=0
    g6: LineSegment StartX=-11.25 StartY=-19.5 StartZ=0 EndX=-10.25 EndY=-19.5 EndZ=0
    g7: LineSegment StartX=-10.25 StartY=-19.5 StartZ=0 EndX=-10.25 EndY=-12.9 EndZ=0
    g8: Circle [constr] CenterX=0 CenterY=-24 CenterZ=0 NormalX=0 NormalY=0 NormalZ=1 AngleXU=0 Radius=3
    g9: LineSegment StartX=4.5 StartY=-24 StartZ=0 EndX=11.5 EndY=-24 EndZ=0
    g10: LineSegment StartX=11.5 StartY=-24 StartZ=0 EndX=11.5 EndY=-22.8 EndZ=0
    g11: LineSegment StartX=10.5 StartY=-21.8 StartZ=0 EndX=5.5 EndY=-21.8 EndZ=0
    g12: LineSegment StartX=4.5 StartY=-22.8 StartZ=0 EndX=4.5 EndY=-24 EndZ=0
    g13: ArcOfCircle CenterX=5.5 CenterY=-22.8 CenterZ=0 NormalX=0 NormalY=0 NormalZ=1 AngleXU=0 Radius=1 StartAngle=1.5708 EndAngle=3.14159
    g14: ArcOfCircle CenterX=10.5 CenterY=-22.8 CenterZ=0 NormalX=0 NormalY=0 NormalZ=1 AngleXU=0 Radius=1 StartAngle=7e-16 EndAngle=1.5708
  constraints (42):
    c: Coincident(g0,g1)
    c: Coincident(g1,g2)
    c: Coincident(g2,g3)
    c: Coincident(g3,g0)
    c: Horizontal(g0)
    c: Horizontal(g2)
    c: Vertical(g1)
    c: Vertical(g3)
    c: Coincident(g4,g5)
    c: Coincident(g5,g6)
    c: Coincident(g6,g7)
    c: Coincident(g7,g4)
    c: Horizontal(g4)
    c: Horizontal(g6)
    c: Vertical(g5)
    c: Vertical(g7)
    c: Equal(g7,g1)
    c: Equal(g4,g0)
    c: DistanceX(g4,g4) = 1
    c: DistanceY(g3,g3) = 6.6
    c: PointOnObject(g8,g-2)
    c: Radius(g8) = 3
    c: DistanceY(g8,g-1) = 24
    c: DistanceY(g8,g1) = 4.5
    c: DistanceX(g6,g1) = 21.5
    c: Symmetric(g4,g0,g-2)
    c: Coincident(g9,g10)
    c: Coincident(g12,g9)
    c: Horizontal(g9)
    c: Horizontal(g11)
    c: Vertical(g10)
    c: Vertical(g12)
    c: Tangent(g12,g13) = -1.5708
    c: Tangent(g11,g13) = -1.5708
    c: Tangent(g11,g14) = -1.5708
    c: Tangent(g10,g14) = -1.5708
    c: DistanceX(g9,g9) = 7
    c: DistanceY(g9,g11) = 2.2
    c: DistanceX(g8,g9) = 4.5
    c: Equal(g13,g14)
    c: Radius(g14) = 1
    c: DistanceY(g8,g9) = 0
FEATURE [Sketcher::SketchObject] Sketch029  label="SketchAccess"
  AttachmentOffset = pos=(0,0,-41) rot=(0,0,1;0rad)
  FullyConstrained = true
  MapMode = 5
  Placement = pos=(0,41,9.1e-15) rot=(1,0,0;1.5708rad)
  Support = -> [XZ_Plane005]
  expr: .AttachmentOffset.Base.z = -<<param>>.mid_depth / 2
  expr: .Constraints[17] = <<param>>.terminal_seperation + <<param>>.terminal_thickness * 2
  expr: .Constraints[25] = <<param>>.terminal_offset - 1
  expr: .Constraints[5] = <<param>>.bottom_height
  sketch-geometry (9):
    g0: LineSegment StartX=-11.75 StartY=-0.5 StartZ=0 EndX=-11.75 EndY=-20.5 EndZ=0
    g1: LineSegment StartX=-7.95 StartY=-0.5 StartZ=0 EndX=-7.95 EndY=-20.5 EndZ=0
    g2: LineSegment StartX=7.95 StartY=-0.5 StartZ=0 EndX=7.95 EndY=-20.5 EndZ=0
    g3: LineSegment StartX=11.75 StartY=-0.5 StartZ=0 EndX=11.75 EndY=-20.5 EndZ=0
    g4: Circle [constr] CenterX=0 CenterY=-24 CenterZ=0 NormalX=0 NormalY=0 NormalZ=1 AngleXU=0 Radius=3
    g5: LineSegment StartX=-11.75 StartY=-20.5 StartZ=0 EndX=-7.95 EndY=-20.5 EndZ=0
    g6: LineSegment StartX=-11.75 StartY=-0.5 StartZ=0 EndX=-7.95 EndY=-0.5 EndZ=0
    g7: LineSegment StartX=7.95 StartY=-0.5 StartZ=0 EndX=11.75 EndY=-0.5 EndZ=0
    g8: LineSegment StartX=7.95 StartY=-20.5 StartZ=0 EndX=11.75 EndY=-20.5 EndZ=0
  constraints (26):
    c: Vertical(g0)
    c: Vertical(g2)
    c: Equal(g1,g2)
    c: PointOnObject(g4,g-2)
    c: Radius(g4) = 3
    c: DistanceY(g4,g-1) = 24
    c: Coincident(g5,g0)
    c: Coincident(g5,g1)
    c: Coincident(g6,g0)
    c: Coincident(g6,g1)
    c: Horizontal(g6)
    c: Coincident(g7,g2)
    c: Coincident(g7,g3)
    c: Horizontal(g7)
    c: Coincident(g8,g2)
    c: Coincident(g8,g3)
    c: Horizontal(g8)
    c: DistanceX(g0,g3) = 23.5
    c: Vertical(g3)
    c: Equal(g7,g6)
    c: DistanceY(g3,g3) = 20
    c: Symmetric(g1,g2,g-2)
    c: DistanceX(g6,g6) = 3.8
    c: Vertical(g1)
    c: Horizontal(g5)
    c: DistanceY(g4,g1) = 3.5
FEATURE [Sketcher::SketchObject] Sketch030  label="SketchFront"
  AttachmentOffset = pos=(0,0,41) rot=(0,0,1;0rad)
  FullyConstrained = true
  MapMode = 5
  Placement = pos=(0,-41,-9.1e-15) rot=(1,0,0;1.5708rad)
  Support = -> [XZ_Plane006]
  expr: .AttachmentOffset.Base.z = <<param>>.mid_depth / 2
  expr: .Constraints[10] = <<param>>.front_width2
  expr: .Constraints[11] = <<param>>.front_width2
  expr: .Constraints[12] = <<param>>.front_height + 2
  expr: .Constraints[24] = <<param>>.radius_big * 1.2
  expr: .Constraints[25] = <<param>>.radius_big
  expr: .Constraints[6] = <<param>>.radius_small
  expr: .Constraints[7] = <<param>>.bottom_width
  expr: .Constraints[9] = <<param>>.bottom_height
  sketch-geometry (12):
    g0: LineSegment StartX=-47 StartY=42 StartZ=0 EndX=47 EndY=42 EndZ=0
    g1: LineSegment StartX=47 StartY=42 StartZ=0 EndX=47 EndY=9.3923 EndZ=0
    g2: LineSegment StartX=36 StartY=-9.66025 StartZ=0 EndX=36 EndY=-21 EndZ=0
    g3: LineSegment StartX=33 StartY=-24 StartZ=0 EndX=-33 EndY=-24 EndZ=0
    g4: LineSegment StartX=-36 StartY=-21 StartZ=0 EndX=-36 EndY=-9.66025 EndZ=0
    g5: LineSegment StartX=-47 StartY=9.3923 StartZ=0 EndX=-47 EndY=42 EndZ=0
    g6: ArcOfCircle CenterX=-33 CenterY=-21 CenterZ=0 NormalX=0 NormalY=0 NormalZ=1 AngleXU=0 Radius=3 StartAngle=3.14159 EndAngle=4.71239
    g7: ArcOfCircle CenterX=33 CenterY=-21 CenterZ=0 NormalX=0 NormalY=0 NormalZ=1 AngleXU=0 Radius=3 StartAngle=4.71239 EndAngle=6.28319
    g8: ArcOfCircle CenterX=46 CenterY=-9.66025 CenterZ=0 NormalX=0 NormalY=0 NormalZ=1 AngleXU=0 Radius=10 StartAngle=2.0944 EndAngle=3.14159
    g9: ArcOfCircle CenterX=35 CenterY=9.3923 CenterZ=0 NormalX=0 NormalY=0 NormalZ=1 AngleXU=0 Radius=12 StartAngle=5.23599 EndAngle=6.28319
    g10: ArcOfCircle CenterX=-46 CenterY=-9.66025 CenterZ=0 NormalX=0 NormalY=0 NormalZ=1 AngleXU=0 Radius=10 StartAngle=0 EndAngle=1.0472
    g11: ArcOfCircle CenterX=-35 CenterY=9.3923 CenterZ=0 NormalX=0 NormalY=0 NormalZ=1 AngleXU=0 Radius=12 StartAngle=3.14159 EndAngle=4.18879
  constraints (30):
    c: Vertical(g2)
    c: Vertical(g4)
    c: Tangent(g4,g6) = 1.5708
    c: Tangent(g3,g6) = 1.5708
    c: Tangent(g3,g7) = 1.5708
    c: Tangent(g2,g7) = 1.5708
    c: Radius(g7) = 3
    c: DistanceX(g4,g2) = 72
    c: Symmetric(g3,g3,g-2)
    c: DistanceY(g3,g-1) = 24
    c: DistanceX(g5,g1) = 94
    c: DistanceX(g5,g1) = 94
    c: DistanceY(g3,g0) = 66
    c: Equal(g7,g6)
    c: Symmetric(g5,g1,g-2)
    c: Equal(g4,g2)
    c: Coincident(g0,g1)
    c: Coincident(g5,g0)
    c: Symmetric(g0,g0,g-2)
    c: Tangent(g10,g4) = -1.5708
    c: Tangent(g8,g2) = -1.5708
    c: Coincident(g11,g10)
    c: DistanceY(g8,g-1) = 1
    c: Equal(g9,g11)
    c: Radius(g9) = 12
    c: Radius(g8) = 10
    c: Equal(g8,g10)
    c: Tangent(g11,g5) = 1.5708
    c: Tangent(g1,g9) = 1.5708
    c: Tangent(g8,g9) = 1.5708
FEATURE [Sketcher::SketchObject] Sketch031  label="SketchRear"
  AttachmentOffset = pos=(0,0,-46) rot=(0,0,1;0rad)
  FullyConstrained = true
  MapMode = 5
  Placement = pos=(0,46,1.02e-14) rot=(1,0,0;1.5708rad)
  Support = -> [XZ_Plane006]
  expr: .AttachmentOffset.Base.z = -<<param>>.mid_depth / 2 - <<param>>.back_thickness
  expr: .Constraints[15] = <<param>>.front_height + 2
  expr: .Constraints[1] = <<param>>.radius_small
  expr: .Constraints[2] = <<param>>.bottom_height
  expr: .Constraints[3] = <<param>>.rear_width
  sketch-geometry (6):
    g0: LineSegment StartX=-33 StartY=-24 StartZ=0 EndX=33 EndY=-24 EndZ=0
    g1: LineSegment StartX=36 StartY=42 StartZ=0 EndX=-36 EndY=42 EndZ=0
    g2: ArcOfCircle CenterX=-33 CenterY=-21 CenterZ=0 NormalX=0 NormalY=0 NormalZ=1 AngleXU=0 Radius=3 StartAngle=3.14159 EndAngle=4.71239
    g3: ArcOfCircle CenterX=33 CenterY=-21 CenterZ=0 NormalX=0 NormalY=0 NormalZ=1 AngleXU=0 Radius=3 StartAngle=4.71239 EndAngle=6.28319
    g4: LineSegment StartX=36 StartY=-21 StartZ=0 EndX=36 EndY=42 EndZ=0
    g5: LineSegment StartX=-36 StartY=-21 StartZ=0 EndX=-36 EndY=42 EndZ=0
  constraints (19):
    c: Horizontal(g0)
    c: Radius(g3) = 3
    c: DistanceY(g0,g-1) = 24
    c: DistanceX(g2,g3) = 72
    c: Coincident(g4,g3)
    c: Vertical(g4)
    c: Coincident(g5,g2)
    c: Equal(g5,g4)
    c: Horizontal(g3,g3)
    c: Horizontal(g2,g2)
    c: Equal(g2,g3)
    c: Coincident(g0,g2)
    c: Coincident(g0,g3)
    c: Vertical(g2,g0)
    c: Vertical(g5)
    c: DistanceY(g0,g1) = 66
    c: Symmetric(g4,g5,g-2)
    c: Coincident(g4,g1)
    c: Coincident(g5,g1)
FEATURE [Part::Plane] Plane002  label="Plane"
  AttacherType = Attacher::AttachEngine3D
  Length = 152
  Placement = pos=(-75,41,-75) rot=(1,0,0;1.5708rad)
  Support = -> [XZ_Plane006]
  Width = 150
  expr: .Placement.Base.y = <<param>>.mid_depth / 2
FEATURE [Sketcher::SketchObject] Sketch032  label="SketchBack"
  FullyConstrained = true
  MapMode = 5
  Placement = pos=(0,0,0) rot=(1,0,0;1.5708rad)
  Support = -> [XZ_Plane]
  expr: .Constraints[10] = <<param>>.rear_screw_width1
  expr: .Constraints[11] = <<param>>.reart_screw_width2
  expr: .Constraints[12] = <<param>>.rear_screw_height
  expr: .Constraints[15] = <<param>>.rear_screw_offset
  expr: .Constraints[1] = <<param>>.bottom_height
  expr: .Constraints[2] = <<param>>.rear_width
  expr: .Constraints[9] = <<param>>.screw_hole + 1
  sketch-geometry (6):
    g0: LineSegment [constr] StartX=36 StartY=-24 StartZ=0 EndX=-36 EndY=-24 EndZ=0
    g1: Circle CenterX=-29 CenterY=8.9 CenterZ=0 NormalX=0 NormalY=0 NormalZ=1 AngleXU=0 Radius=1.75
    g2: Circle CenterX=0 CenterY=8.9 CenterZ=0 NormalX=0 NormalY=0 NormalZ=1 AngleXU=0 Radius=1.75
    g3: Circle CenterX=29 CenterY=8.9 CenterZ=0 NormalX=0 NormalY=0 NormalZ=1 AngleXU=0 Radius=1.75
    g4: Circle CenterX=-27.5 CenterY=-16.6 CenterZ=0 NormalX=0 NormalY=0 NormalZ=1 AngleXU=0 Radius=1.75
    g5: Circle CenterX=27.5 CenterY=-16.6 CenterZ=0 NormalX=0 NormalY=0 NormalZ=1 AngleXU=0 Radius=1.75
  constraints (16):
    c: Symmetric(g0,g0,g-2)
    c: DistanceY(g0,g-1) = 24
    c: DistanceX(g0,g0) = 72
    c: Symmetric(g1,g3,g-2)
    c: Symmetric(g4,g5,g-2)
    c: Equal(g4,g1)
    c: Equal(g1,g2)
    c: Equal(g2,g3)
    c: Equal(g3,g5)
    c: Diameter(g1) = 3.5
    c: DistanceX(g1,g3) = 58
    c: DistanceX(g4,g5) = 55
    c: DistanceY(g5,g3) = 25.5
    c: Horizontal(g1,g2)
    c: PointOnObject(g2,g-2)
    c: DistanceY(g0,g5) = 7.4
FEATURE [Part::Loft] Loft
  Closed = false
  MaxDegree = 5
  Ruled = false
  Sections = -> [Sketch030,Sketch031]
  Solid = true
FEATURE [Part::Extrusion] Extrude
  Base = -> Sketch012
  Dir = (1,-1e-16,1e-16)
  DirMode = 2
  FaceMakerClass = Part::FaceMakerBullseye
  InnerTaperAngle = 0
  InnerTaperAngleRev = 0
  LengthFwd = 100
  LengthRev = 0
  Solid = true
  Symmetric = true
FEATURE [Part::MultiCommon] Common
  Shapes = -> [Extrude,Loft]
FEATURE [Part::FeaturePython] Slice  # WARN: FeaturePython — macro-defined, semantics opaque (R4)
  Base = -> Common
  Mode = 1
  Tolerance = 0
  Tools = -> [Plane002]
FEATURE [Part::FeaturePython] Slice_child0  label="Slice.0"  # WARN: FeaturePython — macro-defined, semantics opaque (R4)
  Base = -> Slice
  FilterType = 1
  Invert = false
  OverrideMaxVal = 0
  WindowFrom = 80
  WindowTo = 100
  items = 0
FEATURE [Part::FeaturePython] Slice_child1  label="Slice.1"  # WARN: FeaturePython — macro-defined, semantics opaque (R4)
  Base = -> Slice
  FilterType = 1
  Invert = false
  OverrideMaxVal = 0
  WindowFrom = 80
  WindowTo = 100
  items = 1
FEATURE [App::DocumentObjectGroup] GrExplode_Slice  label="Exploded Slice"
  ExportMode = 1
  Group = -> [Slice_child0,Slice_child1]
  _GroupVersion = 1
FEATURE [App::DocumentObjectGroup] Group001  label="BaseShape"
  ExportMode = 1
  Group = -> [Common,Sketch012,Sketch031,Sketch030,Plane002,GrExplode_Slice]
  _GroupVersion = 1
FEATURE [PartDesign::FeatureBase] BaseFeature
  BaseFeature = -> Slice_child1
  NewSolid = false
  Suppress = false
FEATURE [PartDesign::Pocket] Pocket
  BaseFeature = -> BaseFeature
  ClaimChildren = false
  Fit = 0
  FitJoin = 0
  InnerFit = 0
  InnerFitJoin = 0
  InnerTaperAngle = 0
  InnerTaperAngleRev = 0
  Length = 5
  Length2 = 100
  Midplane = true
  NewSolid = false
  Profile = -> Sketch032
  Suppress = false
  Type = 1
FEATURE [PartDesign::Fillet] Fillet
  Base = -> Pocket [Edge30,Edge63]
  BaseFeature = -> Pocket
  NewSolid = false
  Radius = 10
  SupportTransform = false
  Suppress = false
  expr: Radius = <<param>>.radius_big
FEATURE [PartDesign::FeatureBase] BaseFeature001
  BaseFeature = -> Slice_child0
  NewSolid = false
  Suppress = false
FEATURE [PartDesign::Pocket] Pocket001  label="PocketBatt"
  BaseFeature = -> BaseFeature001
  ClaimChildren = false
  Fit = 0
  FitJoin = 0
  InnerFit = 0
  InnerFitJoin = 0
  InnerTaperAngle = 0
  InnerTaperAngleRev = 0
  Length = 14.6
  Length2 = 100
  NewSolid = false
  Profile = -> Sketch018
  Reversed = true
  Suppress = false
  Type = 0
  expr: Length = <<param>>.batt_carveout
FEATURE [PartDesign::Pad] Pad  label="PadBatt"
  BaseFeature = -> Pocket001
  ClaimChildren = false
  Direction = (1,1,1)
  Fit = 0
  FitJoin = 0
  InnerFit = 0
  InnerFitJoin = 0
  InnerTaperAngle = 0
  InnerTaperAngleRev = 0
  Length = 45
  Length2 = 100
  NewSolid = false
  Profile = -> Sketch019
  Suppress = false
  Type = 0
  expr: Length = <<param>>.batt_rail_length
FEATURE [PartDesign::Pocket] Pocket002  label="PocketSupport"
  BaseFeature = -> Pad
  ClaimChildren = false
  Fit = 0
  FitJoin = 0
  InnerFit = 0
  InnerFitJoin = 0
  InnerTaperAngle = 0
  InnerTaperAngleRev = 0
  Length = 5
  Length2 = 100
  NewSolid = false
  Profile = -> Sketch
  Suppress = false
  Type = 0
FEATURE [PartDesign::Pocket] Pocket006  label="PocketTerminal"
  BaseFeature = -> Pocket002
  ClaimChildren = false
  Fit = 0
  FitJoin = 0
  InnerFit = 0
  InnerFitJoin = 0
  InnerTaperAngle = 0
  InnerTaperAngleRev = 0
  Length = 5
  Length2 = 100
  Midplane = true
  NewSolid = false
  Profile = -> Sketch028
  Suppress = false
  Type = 1
FEATURE [PartDesign::Pocket] Pocket005  label="PocketAccess"
  BaseFeature = -> Pocket006
  ClaimChildren = false
  Fit = 0
  FitJoin = 0
  InnerFit = 0
  InnerFitJoin = 0
  InnerTaperAngle = 0
  InnerTaperAngleRev = 0
  Length = 22
  Length2 = 100
  NewSolid = false
  Profile = -> Sketch029
  Reversed = true
  Suppress = false
  Type = 0
  expr: Length = <<param>>.terminal_depth
FEATURE [PartDesign::SubtractiveLoft] SubtractiveLoft
  BaseFeature = -> Pocket005
  ClaimChildren = false
  Closed = false
  Fit = 0
  FitJoin = 0
  InnerFit = 0
  InnerFitJoin = 0
  NewSolid = false
  Profile = -> Sketch022
  Ruled = true
  Sections = -> [Sketch025,Sketch023]
  Suppress = false
FEATURE [PartDesign::Revolution] Revolution  label="RevolutionButton"
  Angle = 360
  Axis = (-1e-16,0.292372,0.956305)
  Base = (-3.1e-15,10,24)
  BaseFeature = -> SubtractiveLoft
  ClaimChildren = false
  Fit = 0
  FitJoin = 0
  InnerFit = 0
  InnerFitJoin = 0
  NewSolid = false
  Profile = -> Sketch021
  ReferenceAxis = -> Sketch021 [V_Axis]
  Reversed = true
  Suppress = false
FEATURE [PartDesign::Pocket] Pocket007  label="PocketButton"
  BaseFeature = -> Revolution
  ClaimChildren = false
  Fit = 0
  FitJoin = 0
  InnerFit = 0
  InnerFitJoin = 0
  InnerTaperAngle = 0
  InnerTaperAngleRev = 0
  Length = 14
  Length2 = 100
  NewSolid = false
  Profile = -> Sketch008
  Reversed = true
  Suppress = false
  Type = 0
FEATURE [PartDesign::Groove] Groove  label="GrooveButton"
  Angle = 360
  Axis = (-1e-16,0.292372,0.956305)
  Base = (-2.7e-15,10,22)
  BaseFeature = -> Pocket007
  ClaimChildren = false
  Fit = 0
  FitJoin = 0
  InnerFit = 0
  InnerFitJoin = 0
  NewSolid = false
  Profile = -> Sketch027
  ReferenceAxis = -> Sketch027 [V_Axis]
  Suppress = false
FEATURE [PartDesign::Pocket] Pocket004  label="PocketFrontScrews"
  BaseFeature = -> Groove
  ClaimChildren = false
  Fit = 0
  FitJoin = 0
  InnerFit = 0
  InnerFitJoin = 0
  InnerTaperAngle = 0
  InnerTaperAngleRev = 0
  Length = 5
  Length2 = 100
  NewSolid = false
  Profile = -> Sketch026
  Suppress = false
  Type = 0
FEATURE [PartDesign::Pocket] Pocket003  label="PocketFace"
  BaseFeature = -> Pocket004
  ClaimChildren = false
  Fit = 0
  FitJoin = 0
  InnerFit = 0
  InnerFitJoin = 0
  InnerTaperAngle = 0
  InnerTaperAngleRev = 0
  Length = 3.1
  Length2 = 100
  NewSolid = false
  Profile = -> Sketch024
  Reversed = true
  Suppress = false
  Type = 0
  expr: Length = <<param>>.face_thickness + 0.1
FEATURE [Sketcher::SketchObject] Sketch033  label="SketchFace"
  AttachmentOffset = pos=(0,0,38) rot=(1,0,0;-0.349066rad)
  FullyConstrained = false
  MapMode = 5
  Placement = pos=(0,-38,-8.4e-15) rot=(-1,0,0;5.06145rad)
  Support = -> [XZ_Plane007]
  expr: .AttachmentOffset.Base.z = <<param>>.mid_depth / 2 - <<param>>.face_thickness
  expr: .AttachmentOffset.Rotation.Angle = -<<param>>.front_angle
  expr: .Constraints[12] = <<param>>.face_radius
  expr: .Constraints[21] = <<param>>.face_width1 - 0.2
  expr: .Constraints[22] = <<param>>.face_width2 - 0.2
  expr: .Constraints[23] = <<param>>.face_height - 0.2
  expr: .Constraints[27] = <<param>>.screw_hole + 1
  expr: .Constraints[28] = <<param>>.front_screw_width2 / 2
  expr: .Constraints[29] = <<param>>.front_screw_width2 / 2
  expr: .Constraints[30] = <<param>>.front_screw_width1 / 2
  expr: .Constraints[31] = <<param>>.front_screw_width1 / 2
  expr: .Constraints[32] = <<param>>.front_screw_height
  expr: .Constraints[35] = <<param>>.front_screw_offset + <<param>>.face_offset
  expr: .Constraints[48] = <<param>>.face_offset
  sketch-geometry (22):
    g0: LineSegment StartX=-34.4064 StartY=37.6 StartZ=0 EndX=34.4064 EndY=37.6 EndZ=0
    g1: LineSegment StartX=42.4 StartY=29.9189 StartZ=0 EndX=43.15 EndY=11.1189 EndZ=0
    g2: LineSegment StartX=35.1564 StartY=2.8 StartZ=0 EndX=-35.1564 EndY=2.8 EndZ=0
    g3: LineSegment StartX=-43.15 StartY=11.1189 StartZ=0 EndX=-42.4 EndY=29.9189 EndZ=0
    g4: ArcOfCircle CenterX=34.4064 CenterY=29.6 CenterZ=0 NormalX=0 NormalY=0 NormalZ=1 AngleXU=0 Radius=8 StartAngle=0.0398724 EndAngle=1.5708
    g5: ArcOfCircle CenterX=35.1564 CenterY=10.8 CenterZ=0 NormalX=0 NormalY=0 NormalZ=1 AngleXU=0 Radius=8 StartAngle=4.71239 EndAngle=6.32306
    g6: ArcOfCircle CenterX=-34.4064 CenterY=29.6 CenterZ=0 NormalX=0 NormalY=0 NormalZ=1 AngleXU=0 Radius=8 StartAngle=1.5708 EndAngle=3.10172
    g7: ArcOfCircle CenterX=-35.1564 CenterY=10.8 CenterZ=0 NormalX=0 NormalY=0 NormalZ=1 AngleXU=0 Radius=8 StartAngle=3.10172 EndAngle=4.71239
    g8: Circle CenterX=-36.75 CenterY=32.3 CenterZ=0 NormalX=0 NormalY=0 NormalZ=1 AngleXU=0 Radius=1.75
    g9: Circle CenterX=36.75 CenterY=32.3 CenterZ=0 NormalX=0 NormalY=0 NormalZ=1 AngleXU=0 Radius=1.75
    g10: Circle CenterX=-38 CenterY=8.3 CenterZ=0 NormalX=0 NormalY=0 NormalZ=1 AngleXU=0 Radius=1.75
    g11: Circle CenterX=38 CenterY=8.3 CenterZ=0 NormalX=0 NormalY=0 NormalZ=1 AngleXU=0 Radius=1.75
    g12: LineSegment StartX=-13.0096 StartY=27.8956 StartZ=0 EndX=13.1337 EndY=27.8956 EndZ=0
    g13: LineSegment StartX=16.3841 StartY=24.6453 StartZ=0 EndX=16.3841 EndY=12.0136 EndZ=0
    g14: LineSegment StartX=13.3937 StartY=9.02319 StartZ=0 EndX=-13.746 EndY=9.02319 EndZ=0
    g15: LineSegment StartX=-17.1772 StartY=12.4543 StartZ=0 EndX=-17.1772 EndY=23.728 EndZ=0
    g16: ArcOfCircle CenterX=-13.0096 CenterY=23.728 CenterZ=0 NormalX=0 NormalY=0 NormalZ=1 AngleXU=0 Radius=4.16762 StartAngle=1.5708 EndAngle=3.14159
    g17: ArcOfCircle CenterX=-13.746 CenterY=12.4543 CenterZ=0 NormalX=0 NormalY=0 NormalZ=1 AngleXU=0 Radius=3.43115 StartAngle=3.14159 EndAngle=4.71239
    g18: ArcOfCircle CenterX=13.3937 CenterY=12.0136 CenterZ=0 NormalX=0 NormalY=0 NormalZ=1 AngleXU=0 Radius=2.99038 StartAngle=4.71239 EndAngle=6.28319
    g19: ArcOfCircle CenterX=13.1337 CenterY=24.6453 CenterZ=0 NormalX=0 NormalY=0 NormalZ=1 AngleXU=0 Radius=3.25034 StartAngle=0 EndAngle=1.5708
    g20: Circle CenterX=-29.7683 CenterY=20.7999 CenterZ=0 NormalX=0 NormalY=0 NormalZ=1 AngleXU=0 Radius=4.79642
    g21: Circle CenterX=27.9802 CenterY=19.4899 CenterZ=0 NormalX=0 NormalY=0 NormalZ=1 AngleXU=0 Radius=6.72016
  constraints (51):
    c: Coincident(g4,g0)
    c: Coincident(g4,g1)
    c: Coincident(g5,g1)
    c: Coincident(g5,g2)
    c: Coincident(g6,g0)
    c: Coincident(g6,g3)
    c: Coincident(g7,g3)
    c: Coincident(g7,g2)
    c: Equal(g1,g3)
    c: Equal(g4,g6)
    c: Equal(g6,g7)
    c: Equal(g7,g5)
    c: Radius(g4) = 8
    c: Tangent(g6,g3)
    c: Tangent(g7,g3)
    c: Tangent(g7,g2)
    c: Tangent(g6,g0)
    c: Tangent(g4,g0)
    c: Tangent(g4,g1)
    c: Tangent(g5,g1)
    c: Tangent(g5,g2)
    c: DistanceX(g3,g1) = 84.8
    c: DistanceX(g3,g1) = 86.3
    c: DistanceY(g2,g0) = 34.8
    c: Equal(g9,g8)
    c: Equal(g8,g10)
    c: Equal(g10,g11)
    c: Diameter(g8) = 3.5
    c: DistanceX(g10,g-1) = 38
    c: DistanceX(g-1,g11) = 38
    c: DistanceX(g-1,g9) = 36.75
    c: DistanceX(g8,g-1) = 36.75
    c: DistanceY(g11,g9) = 24
    c: Horizontal(g8,g9)
    c: Horizontal(g10,g11)
    c: DistanceY(g-1,g11) = 8.3
    c: Horizontal(g12)
    c: Horizontal(g14)
    c: Vertical(g13)
    c: Vertical(g15)
    c: Tangent(g15,g16) = 1.5708
    c: Tangent(g12,g16) = 1.5708
    c: Tangent(g15,g17) = 1.5708
    c: Tangent(g14,g17) = 1.5708
    c: Tangent(g14,g18) = 1.5708
    c: Tangent(g13,g18) = 1.5708
    c: Tangent(g12,g19) = 1.5708
    c: Tangent(g13,g19) = 1.5708
    c: DistanceY(g-1,g2) = 2.8
    c: Horizontal(g0)
    c: Symmetric(g2,g2,g-2)
FEATURE [PartDesign::Pad] Pad001  label="PadFace"
  ClaimChildren = false
  Direction = (1,1,1)
  Fit = 0
  FitJoin = 0
  InnerFit = 0
  InnerFitJoin = 0
  InnerTaperAngle = 0
  InnerTaperAngleRev = 0
  Length = 3
  Length2 = 100
  NewSolid = false
  Placement = pos=(0,0,0) rot=(1,0,0;1.5708rad)
  Profile = -> Sketch033
  Suppress = false
  Type = 0
  expr: Length = <<param>>.face_thickness
FEATURE [PartDesign::Chamfer] Chamfer001
  Angle = 45
  Base = -> Pad001 [Edge34]
  BaseFeature = -> Pad001
  ChamferType = 0
  FlipDirection = false
  NewSolid = false
  Placement = pos=(0,0,0) rot=(1,0,0;1.5708rad)
  Size = 2
  Size2 = 1
  SupportTransform = false
  Suppress = false
FEATURE [PartDesign::Chamfer] Chamfer002
  Angle = 45
  Base = -> Chamfer001 [Edge56,Edge54,Edge55,Edge53]
  BaseFeature = -> Chamfer001
  ChamferType = 0
  FlipDirection = false
  NewSolid = false
  Placement = pos=(0,0,0) rot=(1,0,0;1.5708rad)
  Size = 1.4
  Size2 = 1
  SupportTransform = false
  Suppress = false
FEATURE [PartDesign::Body] Body005  label="BodyOLED Needs Work"
  AutoGroupSolids = false
  ExportMode = 0
  Group = -> [Sketch033,Pad001,Chamfer001,Chamfer002]
  Origin = -> Origin007
  Tip = -> Chamfer002
  _ExportChildren = -> [Pad001,Chamfer001,Chamfer002]
  _GroupVersion = 1
FEATURE [PartDesign::Fillet] Fillet009
  Base = -> Fillet [Edge8]
  BaseFeature = -> Fillet
  NewSolid = false
  Radius = 2.93
  SupportTransform = false
  Suppress = false
FEATURE [PartDesign::Chamfer] Chamfer
  Angle = 45
  Base = -> Fillet009 [Edge43,Edge44,Edge45,Edge71,Edge73]
  BaseFeature = -> Fillet009
  ChamferType = 0
  FlipDirection = false
  NewSolid = false
  Size = 1.4
  Size2 = 1
  SupportTransform = false
  Suppress = false
FEATURE [PartDesign::Body] Body  label="BodyBack"
  AutoGroupSolids = false
  BaseFeature = -> Slice_child1
  ExportMode = 0
  Group = -> [BaseFeature,Sketch032,Pocket,Fillet,Fillet009,Chamfer]
  Origin = -> Origin
  Tip = -> Chamfer
  _ExportChildren = -> [BaseFeature,Pocket,Fillet,Fillet009,Chamfer]
  _GroupVersion = 1
FEATURE [PartDesign::Fillet] Fillet010
  Base = -> Pocket003 [Edge191]
  BaseFeature = -> Pocket003
  NewSolid = false
  Radius = 10
  SupportTransform = false
  Suppress = false
FEATURE [PartDesign::Fillet] Fillet011
  Base = -> Fillet010 [Edge2,Edge5]
  BaseFeature = -> Fillet010
  NewSolid = false
  Radius = 10
  SupportTransform = false
  Suppress = false
  expr: Radius = <<param>>.radius_big
FEATURE [PartDesign::Fillet] Fillet012
  Base = -> Fillet011 [Edge11]
  BaseFeature = -> Fillet011
  NewSolid = false
  Radius = 2
  SupportTransform = false
  Suppress = false
FEATURE [PartDesign::Fillet] Fillet013
  Base = -> Fillet012 [Edge57]
  BaseFeature = -> Fillet012
  NewSolid = false
  Radius = 2
  SupportTransform = false
  Suppress = false
FEATURE [PartDesign::Body] Body004  label="BodyCase"
  AutoGroupSolids = false
  BaseFeature = -> Slice_child0
  ExportMode = 0
  Group = -> [BaseFeature001,Sketch008,Sketch029,Sketch018,Sketch019,Sketch021,Sketch022,Sketch023,Sketch024,Sketch025,Sketch026,Sketch027,Sketch028,Sketch,Pocket001,Pad,Pocket002,Pocket006,Pocket005,SubtractiveLoft,Revolution,Pocket007,Groove,Pocket004,Pocket003,Fillet010,Fillet011,Fillet012,Fillet013]
  Origin = -> Origin005
  Tip = -> Fillet013
  _ExportChildren = -> [BaseFeature001,Pocket001,Pad,Pocket002,Pocket006,Pocket005,SubtractiveLoft,Revolution,Pocket007,Groove,Pocket004,Pocket003,Fillet010,Fillet011,Fillet012,Fillet013]
  _GroupVersion = 1
FEATURE [Mesh::Feature] Mesh  label="BodyCase (Meshed)"
FEATURE [Mesh::Feature] Mesh001  label="BodyBack (Meshed)"
FEATURE [App::DocumentObjectGroup] Group002  label="Mesh"
  ExportMode = 1
  Group = -> [Mesh,Mesh001]
  _GroupVersion = 1
FEATURE [App::Part] Part
  ExportMode = 1
  Group = -> [Extrude,Plane002,Common,Sketch012,Loft,Slice_child1,Slice_child0,Slice,GrExplode_Slice,Sketch030,Sketch031,Group001,Group002,Spreadsheet,Body,Body004,Body005,Mesh,Mesh001]
  Origin = -> Origin006
  _ExportChildren = -> [Group001,Group002,Spreadsheet,Body,Body004,Body005]
  _GroupVersion = 1
